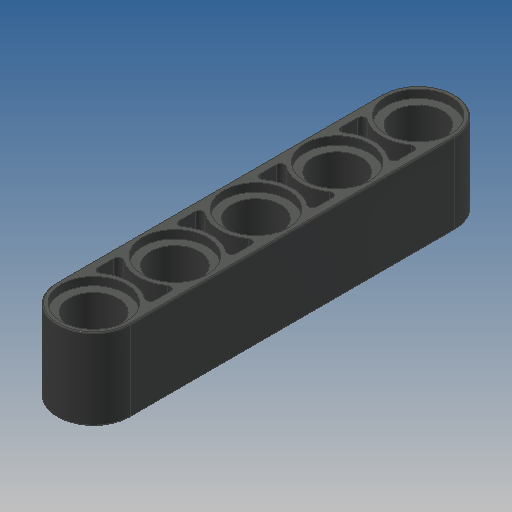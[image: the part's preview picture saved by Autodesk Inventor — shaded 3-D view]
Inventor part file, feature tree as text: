
AUTODESK INVENTOR PART (.ipt)
format: ipt  version: 2022.2 (Build 262287000, 287)  size: 295,424 bytes
history: native  units: mm
features: extrude x3, sketch x2, mirror x1, fillet x1
ambient origin geometry x8: Origin, YZ Plane, XZ Plane, XY Plane, X Axis, Y Axis, Z Axis, Center Point
bodies: Solid1 (feature_tree)
feature tree (7):
  extrude  "Extrusion1"  Depth=6.4mm
  sketch  "Sketch6"  dims[d14=8.0mm d15=0.0mm d32=7.2mm d34=8.0mm d36=0.8mm d41=0.8mm d42=0.0mm d43=3.1mm d44=0.0mm d46=0.4mm d47=0.1mm]
  extrude  "Extrusion7"  Depth=7.2mm
  extrude  "Extrusion8"  Depth=8.0mm
  mirror  "Mirror1"
  fillet  "Fillet1"  Radius=0.8mm
  sketch  "Sketch1"  dims[d8=4.8mm d9=6.4mm]
